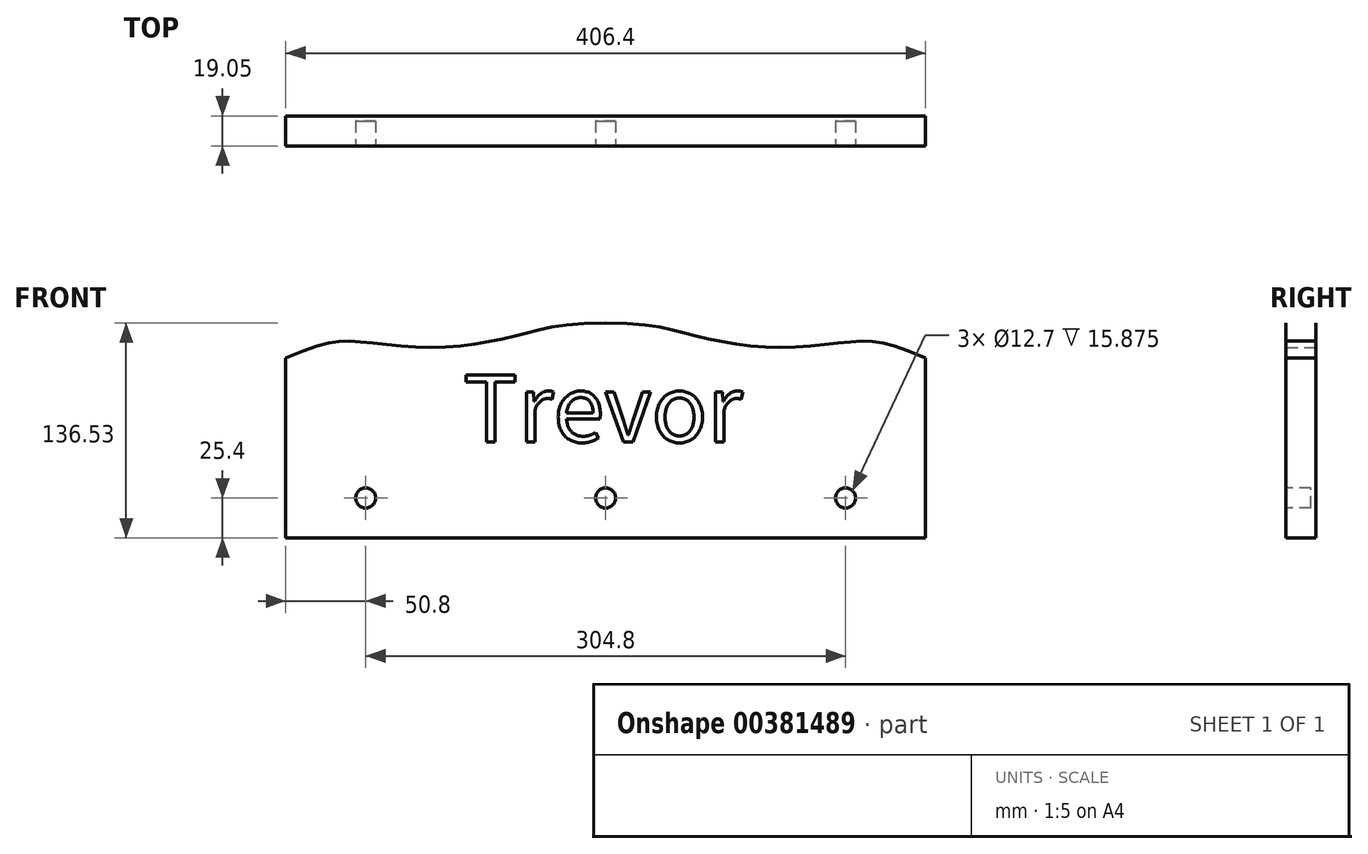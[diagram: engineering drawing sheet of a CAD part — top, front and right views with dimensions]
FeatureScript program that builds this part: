
annotation { "Feature Type Name" : "Feature", "Feature Type Description" : "" }
export const myFeature = defineFeature(function(context is Context, id is Id, definition is map)
    precondition{}
    {
        {
            var Q0;
            Q0=qCreatedBy(makeId("Front.planeOp"),FACE);
            var sketch = newSketch(context, id + "F0", { "sketchPlane" : qUnion([Q0])});
            skLineSegment(sketch, "E0.bottom", {"start": v(-203.2, 0) * mm, "end": v(203.2, 0) * mm});
            skLineSegment(sketch, "E0.left", {"start": v(-203.2, 0) * mm, "end": v(-203.2, 114.3) * mm});
            skLineSegment(sketch, "E0.right", {"start": v(203.2, 0) * mm, "end": v(203.2, 114.3) * mm});
            skFitSpline(sketch, "E1", {"points": [v(-203.2, 114.3) * mm, v(-160.5, 124.93) * mm, v(-111.51, 120.94) * mm, v(-59.05, 127.88) * mm, v(0, 136.53) * mm], "startDerivative": vector(282.43, 122.93) * mm, "endDerivative": vector(347.81, 0.86) * mm});
            skLineSegment(sketch, "E2", {"start": v(0, 136.53) * mm, "end": v(0, 0) * mm, "construction": true});
            skPoint(sketch, "E3.orphan", {"position": v(-203.2, 136.52) * mm});
            skFitSpline(sketch, "E4.MirrorCS", {"points": [v(203.2, 114.3) * mm, v(160.5, 124.93) * mm, v(111.51, 120.94) * mm, v(59.05, 127.88) * mm, v(0, 136.53) * mm], "startDerivative": vector(-282.43, 122.93) * mm, "endDerivative": vector(-347.81, 0.86) * mm});
            skPoint(sketch, "E5.orphan", {"position": v(203.2, 136.53) * mm});
            skSolve(sketch);
        }
        {
            var Q0;
            Q0=qSketchRegion(id+"F0",true);
            extrude(context, id + "F1", {"entities" : qUnion([Q0]), "depth" : 19.05 * mm});
        }
        {
            var Q0;
            Q0=makeQuery(id+"F1.opExtrude","CAP_FACE",FACE,{"disambiguationData":[OSD([sQuery(id+"F0.wireOp",EDGE,"E0.bottom"),sQuery(id+"F0.wireOp",EDGE,"E0.left"),sQuery(id+"F0.wireOp",EDGE,"E0.right"),sQuery(id+"F0.wireOp",EDGE,"E1"),sQuery(id+"F0.wireOp",EDGE,"E4.MirrorCS")])],"isStart":false});
            var sketch = newSketch(context, id + "F2", { "sketchPlane" : qUnion([Q0])});
            skLineSegment(sketch, "E6", {"start": v(0, 0) * mm, "end": v(0, 66.82) * mm, "construction": true});
            skPoint(sketch, "E6.endSnap0", {"position": v(0, 0) * mm});
            skText(sketch, "E7", { "text": "Trevor", "fontName": "NotoSansCJKjp-Regular.otf"});
            const initialGuessF2  = {"E7": [-0.09034, 0.06105, 1, 0, 0.04178]};
            skSetInitialGuess(sketch, initialGuessF2);
            skSolve(sketch);
        }
        {
            var Q0;
            Q0=qSketchRegion(id+"F2",true);
            extrude(context, id + "F3", {"entities" : qUnion([Q0]), "operationType" : NewBodyOperationType.REMOVE, "oppositeDirection" : true, "depth" : 0.3 * mm});
        }
        {
            var Q0;
            {var subQ0=sQuery(id+"F0.wireOp",EDGE,"E0.right");var subQ1=sQuery(id+"F0.wireOp",EDGE,"E4.MirrorCS");var subQ2=sQuery(id+"F0.wireOp",EDGE,"E0.bottom");var subQ3=sQuery(id+"F0.wireOp",EDGE,"E1");var subQ4=sQuery(id+"F0.wireOp",EDGE,"E0.left");Q0=makeQuery(id+"F3.boolean.opBoolean","SPLIT",FACE,{"disambiguationData":[TD([makeQuery(id+"F1.opExtrude","SWEPT_FACE",FACE,{"disambiguationData":[OSD([subQ2])]})])],"derivedFrom":makeQuery(id+"F1.opExtrude","CAP_FACE",FACE,{"disambiguationData":[OSD([subQ2,subQ4,subQ0,subQ3,subQ1])],"isStart":false})});}
            var sketch = newSketch(context, id + "F4", { "sketchPlane" : qUnion([Q0])});
            skCircle(sketch, "E8", {"center": v(0, 25.4) * mm, "radius": 6.35 * mm});
            skCircle(sketch, "E9", {"center": v(-152.4, 25.4) * mm, "radius": 6.35 * mm});
            skCircle(sketch, "E10", {"center": v(152.4, 25.4) * mm, "radius": 6.35 * mm});
            skSolve(sketch);
        }
        {
            var Q0;
            Q0 = qSketchRegion(id + "F4", true);
            extrude(context, id + "F5", {"entities" : qUnion([Q0]), "operationType" : NewBodyOperationType.REMOVE, "oppositeDirection" : true, "depth" : 15.88 * mm});
        }
    });
